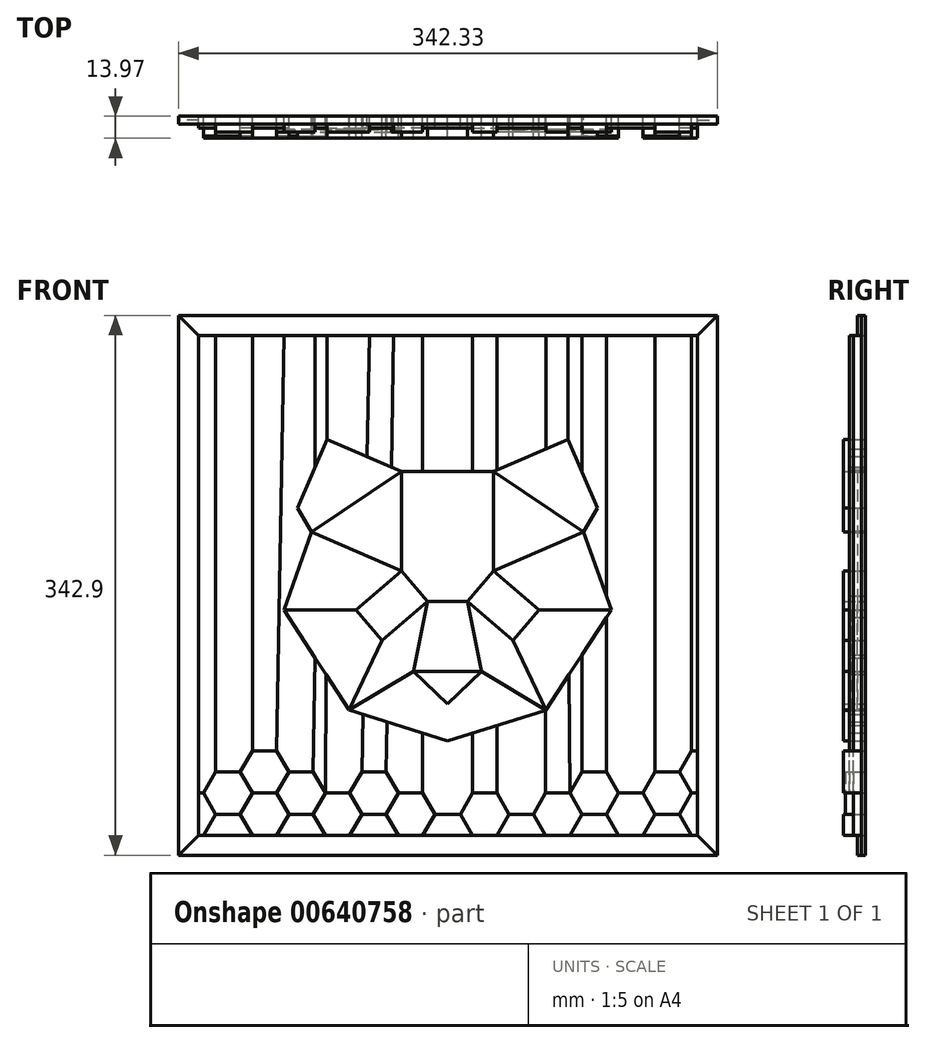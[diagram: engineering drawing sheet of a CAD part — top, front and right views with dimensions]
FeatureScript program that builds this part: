
annotation { "Feature Type Name" : "Feature", "Feature Type Description" : "" }
export const myFeature = defineFeature(function(context is Context, id is Id, definition is map)
    precondition{}
    {
        {
            var Q0;
            Q0=qCreatedBy(makeId("Front.planeOp"),FACE);
            var sketch = newSketch(context, id + "F0", { "sketchPlane" : qUnion([Q0])});
            skLineSegment(sketch, "E0.bottom", {"start": v(-170.79, 187) * mm, "end": v(171.54, 187) * mm});
            skLineSegment(sketch, "E0.top", {"start": v(-170.79, -155.9) * mm, "end": v(171.54, -155.9) * mm});
            skLineSegment(sketch, "E0.left", {"start": v(-170.79, 187) * mm, "end": v(-170.79, -155.9) * mm});
            skLineSegment(sketch, "E1.0", {"start": v(-158.09, 174.3) * mm, "end": v(158.84, 174.3) * mm});
            skLineSegment(sketch, "E2", {"start": v(-158.09, 174.3) * mm, "end": v(-158.09, -143.2) * mm});
            skLineSegment(sketch, "E3", {"start": v(-158.09, 174.3) * mm, "end": v(-170.79, 187) * mm});
            skLineSegment(sketch, "E4", {"start": v(-158.09, -143.2) * mm, "end": v(-15.07, -143.2) * mm});
            skLineSegment(sketch, "E5", {"start": v(-158.09, -143.2) * mm, "end": v(-170.79, -155.9) * mm});
            skLineSegment(sketch, "E6", {"start": v(158.84, 174.3) * mm, "end": v(158.84, -143.2) * mm});
            skLineSegment(sketch, "E7", {"start": v(158.84, 174.3) * mm, "end": v(171.54, 187) * mm});
            skLineSegment(sketch, "E8", {"start": v(158.84, -143.2) * mm, "end": v(171.54, -155.9) * mm});
            skLineSegment(sketch, "E9", {"start": v(171.54, 187) * mm, "end": v(171.54, -155.9) * mm});
            skPoint(sketch, "E10.start.orphan", {"position": v(0.38, 174.3) * mm});
            skLineSegment(sketch, "E11", {"start": v(0, -39.07) * mm, "end": v(21.5, -39.07) * mm});
            skLineSegment(sketch, "E12", {"start": v(21.5, -39.07) * mm, "end": v(0, -59.85) * mm});
            skLineSegment(sketch, "E13", {"start": v(0, 5.38) * mm, "end": v(12.7, 5.38) * mm});
            skLineSegment(sketch, "E14", {"start": v(21.5, -39.07) * mm, "end": v(12.7, 5.38) * mm});
            skLineSegment(sketch, "E15", {"start": v(0, -59.85) * mm, "end": v(0, -83.14) * mm});
            skLineSegment(sketch, "E16", {"start": v(0, -83.14) * mm, "end": v(62.58, -63.7) * mm});
            skLineSegment(sketch, "E17", {"start": v(62.58, -63.7) * mm, "end": v(21.5, -39.07) * mm});
            skLineSegment(sketch, "E18", {"start": v(29.2, 24.68) * mm, "end": v(12.7, 5.38) * mm});
            skLineSegment(sketch, "E19", {"start": v(29.2, 87.93) * mm, "end": v(29.2, 24.68) * mm});
            skLineSegment(sketch, "E20", {"start": v(29.2, 87.93) * mm, "end": v(0, 87.93) * mm});
            skLineSegment(sketch, "E21", {"start": v(29.2, 87.93) * mm, "end": v(76.43, 108.07) * mm});
            skLineSegment(sketch, "E22", {"start": v(12.7, 5.38) * mm, "end": v(41.55, -19.3) * mm});
            skLineSegment(sketch, "E23", {"start": v(41.55, -19.3) * mm, "end": v(58.06, 0) * mm});
            skLineSegment(sketch, "E24", {"start": v(58.06, 0) * mm, "end": v(29.2, 24.68) * mm});
            skLineSegment(sketch, "E25", {"start": v(62.58, -63.7) * mm, "end": v(41.55, -19.3) * mm});
            skLineSegment(sketch, "E26", {"start": v(62.58, -63.7) * mm, "end": v(103.99, 0) * mm});
            skLineSegment(sketch, "E27", {"start": v(103.99, 0) * mm, "end": v(58.06, 0) * mm});
            skLineSegment(sketch, "E28", {"start": v(103.99, 0) * mm, "end": v(86.29, 49.5) * mm});
            skLineSegment(sketch, "E29", {"start": v(86.29, 49.5) * mm, "end": v(29.2, 24.68) * mm});
            skLineSegment(sketch, "E30", {"start": v(29.2, 87.93) * mm, "end": v(86.29, 49.5) * mm});
            skLineSegment(sketch, "E31", {"start": v(86.29, 49.5) * mm, "end": v(95.32, 64.57) * mm});
            skLineSegment(sketch, "E32", {"start": v(95.32, 64.57) * mm, "end": v(76.43, 108.07) * mm});
            skPoint(sketch, "E33.MirrorP", {"position": v(-0.38, 174.3) * mm});
            skLineSegment(sketch, "E34.MirrorCS", {"start": v(0, 5.38) * mm, "end": v(-12.7, 5.38) * mm});
            skLineSegment(sketch, "E35.MirrorCS", {"start": v(-86.29, 49.5) * mm, "end": v(-95.32, 64.57) * mm});
            skLineSegment(sketch, "E36.MirrorCS", {"start": v(-29.2, 87.93) * mm, "end": v(-86.29, 49.5) * mm});
            skLineSegment(sketch, "E37.MirrorCS", {"start": v(-62.58, -63.7) * mm, "end": v(-21.5, -39.07) * mm});
            skLineSegment(sketch, "E38.MirrorCS", {"start": v(-103.99, 0) * mm, "end": v(-58.06, 0) * mm});
            skLineSegment(sketch, "E39.MirrorCS", {"start": v(-29.2, 87.93) * mm, "end": v(-29.2, 24.68) * mm});
            skLineSegment(sketch, "E40.MirrorCS", {"start": v(-62.58, -63.7) * mm, "end": v(-41.55, -19.3) * mm});
            skLineSegment(sketch, "E41.MirrorCS", {"start": v(-12.7, 5.38) * mm, "end": v(-41.55, -19.3) * mm});
            skLineSegment(sketch, "E42.MirrorCS", {"start": v(0, -39.07) * mm, "end": v(-21.5, -39.07) * mm});
            skLineSegment(sketch, "E43.MirrorCS", {"start": v(-86.29, 49.5) * mm, "end": v(-29.2, 24.68) * mm});
            skLineSegment(sketch, "E44.MirrorCS", {"start": v(-95.32, 64.57) * mm, "end": v(-76.43, 108.07) * mm});
            skLineSegment(sketch, "E45.MirrorCS", {"start": v(-21.5, -39.07) * mm, "end": v(-12.7, 5.38) * mm});
            skLineSegment(sketch, "E46.MirrorCS", {"start": v(-29.2, 87.93) * mm, "end": v(0, 87.93) * mm});
            skLineSegment(sketch, "E47.MirrorCS", {"start": v(-29.2, 87.93) * mm, "end": v(-76.43, 108.07) * mm});
            skLineSegment(sketch, "E48.MirrorCS", {"start": v(0, -83.14) * mm, "end": v(-62.58, -63.7) * mm});
            skLineSegment(sketch, "E49.MirrorCS", {"start": v(-29.2, 24.68) * mm, "end": v(-12.7, 5.38) * mm});
            skLineSegment(sketch, "E50.MirrorCS", {"start": v(-21.5, -39.07) * mm, "end": v(0, -59.85) * mm});
            skLineSegment(sketch, "E51.MirrorCS", {"start": v(-41.55, -19.3) * mm, "end": v(-58.06, 0) * mm});
            skLineSegment(sketch, "E52.MirrorCS", {"start": v(-58.06, 0) * mm, "end": v(-29.2, 24.68) * mm});
            skLineSegment(sketch, "E53.MirrorCS", {"start": v(-103.99, 0) * mm, "end": v(-86.29, 49.5) * mm});
            skLineSegment(sketch, "E54.MirrorCS", {"start": v(-62.58, -63.7) * mm, "end": v(-103.99, 0) * mm});
            skLineSegment(sketch, "E55.1", {"start": v(8.1, -129.81) * mm, "end": v(15.83, -143.2) * mm});
            skLineSegment(sketch, "E56.0", {"start": v(15.83, -116.43) * mm, "end": v(31.29, -116.43) * mm});
            skLineSegment(sketch, "E56.1", {"start": v(31.29, -116.43) * mm, "end": v(39.01, -129.81) * mm});
            skLineSegment(sketch, "E56.2", {"start": v(39.01, -129.81) * mm, "end": v(31.29, -143.2) * mm});
            skLineSegment(sketch, "E56.4", {"start": v(15.83, -143.2) * mm, "end": v(8.1, -129.81) * mm});
            skLineSegment(sketch, "E56.5", {"start": v(8.1, -129.81) * mm, "end": v(15.83, -116.43) * mm});
            skLineSegment(sketch, "E57.MirrorCS", {"start": v(54.47, -129.81) * mm, "end": v(39.01, -129.81) * mm});
            skLineSegment(sketch, "E58.MirrorCS", {"start": v(62.2, -143.2) * mm, "end": v(54.47, -129.81) * mm});
            skLineSegment(sketch, "E59.MirrorCS", {"start": v(39.01, -129.81) * mm, "end": v(54.47, -129.81) * mm});
            skLineSegment(sketch, "E60.MirrorCS", {"start": v(54.47, -129.81) * mm, "end": v(62.2, -143.2) * mm});
            skLineSegment(sketch, "E61.MirrorCS", {"start": v(77.65, -143.2) * mm, "end": v(85.38, -129.81) * mm});
            skLineSegment(sketch, "E62.MirrorCS", {"start": v(85.38, -129.81) * mm, "end": v(77.65, -116.43) * mm});
            skLineSegment(sketch, "E63.MirrorCS", {"start": v(77.65, -116.43) * mm, "end": v(62.2, -116.43) * mm});
            skLineSegment(sketch, "E64.MirrorCS", {"start": v(62.2, -116.43) * mm, "end": v(54.47, -129.81) * mm});
            skLineSegment(sketch, "E65.MirrorCS", {"start": v(100.83, -129.81) * mm, "end": v(85.38, -129.81) * mm});
            skLineSegment(sketch, "E66.MirrorCS", {"start": v(108.56, -143.2) * mm, "end": v(100.83, -129.81) * mm});
            skLineSegment(sketch, "E67.trimOffspring", {"start": v(15.83, -143.2) * mm, "end": v(158.84, -143.2) * mm});
            skLineSegment(sketch, "E68.MirrorCS", {"start": v(100.83, -129.81) * mm, "end": v(108.56, -116.43) * mm});
            skLineSegment(sketch, "E69.MirrorCS", {"start": v(108.56, -116.43) * mm, "end": v(124.01, -116.43) * mm});
            skLineSegment(sketch, "E70.MirrorCS", {"start": v(124.01, -116.43) * mm, "end": v(131.74, -129.81) * mm});
            skLineSegment(sketch, "E71.MirrorCS", {"start": v(124.01, -143.2) * mm, "end": v(131.74, -129.81) * mm});
            skLineSegment(sketch, "E72.MirrorCS", {"start": v(147.2, -129.81) * mm, "end": v(131.74, -129.81) * mm});
            skLineSegment(sketch, "E73.MirrorCS", {"start": v(147.2, -129.81) * mm, "end": v(154.92, -143.2) * mm});
            skLineSegment(sketch, "E74.MirrorCS", {"start": v(154.92, -116.43) * mm, "end": v(147.2, -129.81) * mm});
            skLineSegment(sketch, "E75.MirrorCS", {"start": v(158.84, -116.43) * mm, "end": v(154.92, -116.43) * mm});
            skLineSegment(sketch, "E76", {"start": v(15.83, -143.2) * mm, "end": v(-15.07, -143.2) * mm});
            skLineSegment(sketch, "E77.MirrorCS", {"start": v(-62.2, -143.2) * mm, "end": v(-54.47, -129.81) * mm});
            skLineSegment(sketch, "E78.MirrorCS", {"start": v(-158.09, -116.43) * mm, "end": v(-154.92, -116.43) * mm});
            skLineSegment(sketch, "E79.MirrorCS", {"start": v(-54.47, -129.81) * mm, "end": v(-39.01, -129.81) * mm});
            skLineSegment(sketch, "E80.MirrorCS", {"start": v(-54.47, -129.81) * mm, "end": v(-62.2, -143.2) * mm});
            skLineSegment(sketch, "E81.MirrorCS", {"start": v(-15.83, -143.2) * mm, "end": v(-8.1, -129.81) * mm});
            skLineSegment(sketch, "E82.MirrorCS", {"start": v(-124.01, -143.2) * mm, "end": v(-131.74, -129.81) * mm});
            skLineSegment(sketch, "E83.MirrorCS", {"start": v(-39.01, -129.81) * mm, "end": v(-31.29, -143.2) * mm});
            skLineSegment(sketch, "E84.MirrorCS", {"start": v(-31.29, -116.43) * mm, "end": v(-39.01, -129.81) * mm});
            skLineSegment(sketch, "E85.MirrorCS", {"start": v(-147.2, -129.81) * mm, "end": v(-131.74, -129.81) * mm});
            skLineSegment(sketch, "E86.MirrorCS", {"start": v(-100.83, -129.81) * mm, "end": v(-85.38, -129.81) * mm});
            skLineSegment(sketch, "E87.MirrorCS", {"start": v(-8.1, -129.81) * mm, "end": v(-15.83, -116.43) * mm});
            skLineSegment(sketch, "E88.MirrorCS", {"start": v(-108.56, -116.43) * mm, "end": v(-124.01, -116.43) * mm});
            skLineSegment(sketch, "E89.MirrorCS", {"start": v(-8.1, -129.81) * mm, "end": v(-15.83, -143.2) * mm});
            skLineSegment(sketch, "E90.MirrorCS", {"start": v(-85.38, -129.81) * mm, "end": v(-77.65, -116.43) * mm});
            skLineSegment(sketch, "E91.MirrorCS", {"start": v(-147.2, -129.81) * mm, "end": v(-154.92, -143.2) * mm});
            skLineSegment(sketch, "E92.MirrorCS", {"start": v(-77.65, -143.2) * mm, "end": v(-85.38, -129.81) * mm});
            skLineSegment(sketch, "E93.MirrorCS", {"start": v(-15.83, -116.43) * mm, "end": v(-31.29, -116.43) * mm});
            skLineSegment(sketch, "E94.MirrorCS", {"start": v(-108.56, -143.2) * mm, "end": v(-100.83, -129.81) * mm});
            skLineSegment(sketch, "E95.MirrorCS", {"start": v(-62.2, -116.43) * mm, "end": v(-54.47, -129.81) * mm});
            skLineSegment(sketch, "E96.MirrorCS", {"start": v(-100.83, -129.81) * mm, "end": v(-108.56, -116.43) * mm});
            skLineSegment(sketch, "E97.MirrorCS", {"start": v(-39.01, -129.81) * mm, "end": v(-54.47, -129.81) * mm});
            skLineSegment(sketch, "E98.MirrorCS", {"start": v(-124.01, -116.43) * mm, "end": v(-131.74, -129.81) * mm});
            skLineSegment(sketch, "E99.MirrorCS", {"start": v(-154.92, -116.43) * mm, "end": v(-147.2, -129.81) * mm});
            skLineSegment(sketch, "E100.MirrorCS", {"start": v(-77.65, -116.43) * mm, "end": v(-62.2, -116.43) * mm});
            skLineSegment(sketch, "E101", {"start": v(-8.1, -129.81) * mm, "end": v(8.1, -129.81) * mm});
            skLineSegment(sketch, "E102.MirrorCS", {"start": v(-62.2, -116.43) * mm, "end": v(-54.47, -103.04) * mm});
            skLineSegment(sketch, "E103.MirrorCS", {"start": v(-54.47, -129.81) * mm, "end": v(-62.2, -116.43) * mm});
            skLineSegment(sketch, "E104.MirrorCS", {"start": v(-39.01, -103.04) * mm, "end": v(-31.29, -116.43) * mm});
            skLineSegment(sketch, "E105.MirrorCS", {"start": v(-54.47, -103.04) * mm, "end": v(-39.01, -103.04) * mm});
            skLineSegment(sketch, "E106.MirrorCS", {"start": v(-108.56, -116.43) * mm, "end": v(-100.83, -103.04) * mm});
            skLineSegment(sketch, "E107.MirrorCS", {"start": v(-85.38, -103.04) * mm, "end": v(-77.65, -116.43) * mm});
            skLineSegment(sketch, "E108.MirrorCS", {"start": v(-100.83, -103.04) * mm, "end": v(-85.38, -103.04) * mm});
            skLineSegment(sketch, "E109.MirrorCS", {"start": v(-154.92, -116.43) * mm, "end": v(-147.2, -103.04) * mm});
            skLineSegment(sketch, "E110.MirrorCS", {"start": v(-131.74, -103.04) * mm, "end": v(-124.01, -116.43) * mm});
            skLineSegment(sketch, "E111.MirrorCS", {"start": v(-147.2, -103.04) * mm, "end": v(-131.74, -103.04) * mm});
            skLineSegment(sketch, "E112.MirrorCS", {"start": v(-131.74, -103.04) * mm, "end": v(-124.01, -89.66) * mm});
            skLineSegment(sketch, "E113.MirrorCS", {"start": v(-108.56, -89.66) * mm, "end": v(-100.83, -103.04) * mm});
            skLineSegment(sketch, "E114.MirrorCS", {"start": v(-124.01, -89.66) * mm, "end": v(-108.56, -89.66) * mm});
            skLineSegment(sketch, "E115.MirrorCS", {"start": v(124.01, -116.43) * mm, "end": v(131.74, -103.04) * mm});
            skLineSegment(sketch, "E116.MirrorCS", {"start": v(147.2, -103.04) * mm, "end": v(154.92, -116.43) * mm});
            skLineSegment(sketch, "E117.MirrorCS", {"start": v(131.74, -103.04) * mm, "end": v(147.2, -103.04) * mm});
            skLineSegment(sketch, "E118.MirrorCS", {"start": v(154.92, -89.66) * mm, "end": v(147.2, -103.04) * mm});
            skLineSegment(sketch, "E119.MirrorCS", {"start": v(158.84, -89.66) * mm, "end": v(154.92, -89.66) * mm});
            skLineSegment(sketch, "E120.0", {"start": v(85.38, -103.04) * mm, "end": v(100.83, -103.04) * mm});
            skLineSegment(sketch, "E120.1", {"start": v(100.83, -103.04) * mm, "end": v(108.56, -116.43) * mm});
            skLineSegment(sketch, "E120.5", {"start": v(77.65, -116.43) * mm, "end": v(85.38, -103.04) * mm});
            skLineSegment(sketch, "E121", {"start": v(-147.2, -103.04) * mm, "end": v(-147.2, 174.3) * mm});
            skLineSegment(sketch, "E122", {"start": v(-124.01, -89.66) * mm, "end": v(-124.01, 174.3) * mm});
            skLineSegment(sketch, "E123", {"start": v(-108.56, -89.66) * mm, "end": v(-103.99, 174.3) * mm});
            skLineSegment(sketch, "E124", {"start": v(-85.38, -103.04) * mm, "end": v(-84.12, -30.56) * mm});
            skLineSegment(sketch, "E125", {"start": v(-54.47, -103.04) * mm, "end": v(-53.83, -66.41) * mm});
            skLineSegment(sketch, "E126", {"start": v(-39.01, -103.04) * mm, "end": v(-38.46, -71.19) * mm});
            skLineSegment(sketch, "E127", {"start": v(-15.83, -116.43) * mm, "end": v(-15.83, -78.22) * mm});
            skLineSegment(sketch, "E128", {"start": v(15.83, -116.43) * mm, "end": v(15.83, -78.22) * mm});
            skLineSegment(sketch, "E129", {"start": v(31.29, -116.43) * mm, "end": v(31.29, -73.42) * mm});
            skLineSegment(sketch, "E130", {"start": v(62.2, -116.43) * mm, "end": v(62.27, -63.03) * mm});
            skLineSegment(sketch, "E131.trimOffspring", {"start": v(-51, 97.22) * mm, "end": v(-49.67, 174.3) * mm});
            skLineSegment(sketch, "E132.trimOffspring", {"start": v(-15.83, 87.93) * mm, "end": v(-15.83, 174.3) * mm});
            skLineSegment(sketch, "E133.trimOffspring", {"start": v(31.29, 88.81) * mm, "end": v(31.29, 174.3) * mm});
            skLineSegment(sketch, "E134.trimOffspring", {"start": v(15.83, 87.93) * mm, "end": v(15.83, 174.3) * mm});
            skLineSegment(sketch, "E135.trimOffspring", {"start": v(-35.66, 90.68) * mm, "end": v(-34.21, 174.3) * mm});
            skLineSegment(sketch, "E136.trimOffspring", {"start": v(62.48, 102.12) * mm, "end": v(62.58, 174.3) * mm});
            skLineSegment(sketch, "E137", {"start": v(85.38, -103.04) * mm, "end": v(85.38, -28.63) * mm});
            skLineSegment(sketch, "E138", {"start": v(100.83, -103.04) * mm, "end": v(100.83, -4.85) * mm});
            skLineSegment(sketch, "E139", {"start": v(131.74, -103.04) * mm, "end": v(131.74, 174.3) * mm});
            skLineSegment(sketch, "E140", {"start": v(154.92, -89.66) * mm, "end": v(154.92, 174.3) * mm});
            skLineSegment(sketch, "E141.trimOffspring", {"start": v(85.38, 87.47) * mm, "end": v(85.38, 174.3) * mm});
            skLineSegment(sketch, "E142.trimOffspring", {"start": v(85.38, 49.1) * mm, "end": v(85.38, 50.12) * mm});
            skLineSegment(sketch, "E143", {"start": v(-76.43, 108.07) * mm, "end": v(-76.43, 174.3) * mm});
            skLineSegment(sketch, "E144", {"start": v(76.43, 108.07) * mm, "end": v(76.43, 174.3) * mm});
            skLineSegment(sketch, "E145.trimOffspring", {"start": v(-84.12, 90.36) * mm, "end": v(-84.12, 174.3) * mm});
            skLineSegment(sketch, "E146", {"start": v(77.24, -41.14) * mm, "end": v(77.65, -116.43) * mm});
            skLineSegment(sketch, "E147.trimOffspring", {"start": v(-77.24, -41.14) * mm, "end": v(-77.65, -116.43) * mm});
            skLineSegment(sketch, "E148.trimOffspring", {"start": v(100.83, 8.83) * mm, "end": v(100.83, 174.3) * mm});
            skSolve(sketch);
        }
        {
            var Q0;
            Q0=makeQuery(id+"F0.imprint","IMPRINT",FACE,{"disambiguationData":[TD([[makeQuery(id+"F0.imprint","IMPRINT",EDGE,{"derivedFrom":sQuery(id+"F0.wireOp",EDGE,"E0.left")}),1.0]])]});
            var Q1;
            {var subQ0=sQuery(id+"F0.wireOp",EDGE,"E7");Q1=makeQuery(id+"F0.imprint","IMPRINT",FACE,{"disambiguationData":[TD([[makeQuery(id+"F0.imprint","IMPRINT",EDGE,{"derivedFrom":subQ0}),-1.0]])]});}
            extrude(context, id + "F1", {"entities" : qUnion([Q0, Q1]), "depth" : 2.54 * mm, "offsetDistance" : 25.4 * mm});
        }
        {
            var Q0;
            Q0=makeQuery(id+"F0.imprint","IMPRINT",FACE,{"disambiguationData":[TD([[makeQuery(id+"F0.imprint","IMPRINT",EDGE,{"derivedFrom":sQuery(id+"F0.wireOp",EDGE,"E0.bottom")}),-1.0]])]});
            var Q1;
            Q1=makeQuery(id+"F0.imprint","IMPRINT",FACE,{"disambiguationData":[TD([[makeQuery(id+"F0.imprint","IMPRINT",EDGE,{"derivedFrom":sQuery(id+"F0.wireOp",EDGE,"E0.top")}),1.0]])]});
            extrude(context, id + "F2", {"entities" : qUnion([Q0, Q1]), "depth" : 5.08 * mm, "offsetDistance" : 25.4 * mm});
        }
        {
            var Q0;
            {var subQ0=sQuery(id+"F0.wireOp",EDGE,"E78.MirrorCS");Q0=makeQuery(id+"F0.imprint","IMPRINT",FACE,{"disambiguationData":[TD([[makeQuery(id+"F0.imprint","IMPRINT",EDGE,{"derivedFrom":subQ0}),1.0]])]});}
            var Q1;
            Q1=makeQuery(id+"F0.imprint","IMPRINT",FACE,{"disambiguationData":[TD([[makeQuery(id+"F0.imprint","IMPRINT",EDGE,{"derivedFrom":sQuery(id+"F0.wireOp",EDGE,"E114.MirrorCS")}),1.0]])]});
            var Q2;
            {var subQ0=sQuery(id+"F0.wireOp",EDGE,"E143");Q2=makeQuery(id+"F0.imprint","IMPRINT",FACE,{"disambiguationData":[TD([[makeQuery(id+"F0.imprint","IMPRINT",EDGE,{"derivedFrom":subQ0}),1.0]])]});}
            var Q3;
            {var subQ0=sQuery(id+"F0.wireOp",EDGE,"E131.trimOffspring");Q3=makeQuery(id+"F0.imprint","IMPRINT",FACE,{"disambiguationData":[TD([[makeQuery(id+"F0.imprint","IMPRINT",EDGE,{"derivedFrom":subQ0}),-1.0]])]});}
            var Q4;
            {var subQ0=sQuery(id+"F0.wireOp",EDGE,"E132.trimOffspring");Q4=makeQuery(id+"F0.imprint","IMPRINT",FACE,{"disambiguationData":[TD([[makeQuery(id+"F0.imprint","IMPRINT",EDGE,{"derivedFrom":subQ0}),-1.0]])]});}
            var Q5;
            {var subQ0=sQuery(id+"F0.wireOp",EDGE,"E133.trimOffspring");Q5=makeQuery(id+"F0.imprint","IMPRINT",FACE,{"disambiguationData":[TD([[makeQuery(id+"F0.imprint","IMPRINT",EDGE,{"derivedFrom":subQ0}),-1.0]])]});}
            var Q6;
            {var subQ0=sQuery(id+"F0.wireOp",EDGE,"E141.trimOffspring");Q6=makeQuery(id+"F0.imprint","IMPRINT",FACE,{"disambiguationData":[TD([[makeQuery(id+"F0.imprint","IMPRINT",EDGE,{"derivedFrom":subQ0}),1.0]])]});}
            var Q7;
            Q7=makeQuery(id+"F0.imprint","IMPRINT",FACE,{"disambiguationData":[TD([[makeQuery(id+"F0.imprint","IMPRINT",EDGE,{"derivedFrom":sQuery(id+"F0.wireOp",EDGE,"E69.MirrorCS")}),1.0]])]});
            var Q8;
            Q8=makeQuery(id+"F0.imprint","IMPRINT",FACE,{"disambiguationData":[TD([[makeQuery(id+"F0.imprint","IMPRINT",EDGE,{"derivedFrom":sQuery(id+"F0.wireOp",EDGE,"E120.5")}),1.0]])]});
            var Q9;
            Q9=makeQuery(id+"F0.imprint","IMPRINT",FACE,{"disambiguationData":[TD([[makeQuery(id+"F0.imprint","IMPRINT",EDGE,{"derivedFrom":sQuery(id+"F0.wireOp",EDGE,"E56.1")}),1.0]])]});
            var Q10;
            Q10=makeQuery(id+"F0.imprint","IMPRINT",FACE,{"disambiguationData":[TD([[makeQuery(id+"F0.imprint","IMPRINT",EDGE,{"derivedFrom":sQuery(id+"F0.wireOp",EDGE,"E56.5")}),1.0]])]});
            var Q11;
            Q11=makeQuery(id+"F0.imprint","IMPRINT",FACE,{"disambiguationData":[TD([[makeQuery(id+"F0.imprint","IMPRINT",EDGE,{"derivedFrom":sQuery(id+"F0.wireOp",EDGE,"E105.MirrorCS")}),1.0]])]});
            var Q12;
            Q12=makeQuery(id+"F0.imprint","IMPRINT",FACE,{"disambiguationData":[TD([[makeQuery(id+"F0.imprint","IMPRINT",EDGE,{"derivedFrom":sQuery(id+"F0.wireOp",EDGE,"E107.MirrorCS")}),1.0]])]});
            var Q13;
            {var subQ4=sQuery(id+"F0.wireOp",EDGE,"E119.MirrorCS");Q13=makeQuery(id+"F0.imprint","IMPRINT",FACE,{"disambiguationData":[TD([[makeQuery(id+"F0.imprint","IMPRINT",EDGE,{"derivedFrom":subQ4}),-1.0]])]});}
            extrude(context, id + "F3", {"entities" : qUnion([Q0, Q1, Q2, Q3, Q4, Q5, Q6, Q7, Q8, Q9, Q10, Q11, Q12, Q13]), "depth" : 7.62 * mm, "offsetDistance" : 25.4 * mm});
        }
        {
            var Q0;
            Q0=makeQuery(id+"F0.imprint","IMPRINT",FACE,{"disambiguationData":[TD([[makeQuery(id+"F0.imprint","IMPRINT",EDGE,{"derivedFrom":sQuery(id+"F0.wireOp",EDGE,"E111.MirrorCS")}),1.0]])]});
            var Q1;
            {var subQ1=sQuery(id+"F0.wireOp",EDGE,"E35.MirrorCS");Q1=makeQuery(id+"F0.imprint","IMPRINT",FACE,{"disambiguationData":[TD([[makeQuery(id+"F0.imprint","IMPRINT",EDGE,{"derivedFrom":subQ1}),1.0]])]});}
            var Q2;
            {var subQ0=sQuery(id+"F0.wireOp",EDGE,"E131.trimOffspring");Q2=makeQuery(id+"F0.imprint","IMPRINT",FACE,{"disambiguationData":[TD([[makeQuery(id+"F0.imprint","IMPRINT",EDGE,{"derivedFrom":subQ0}),1.0]])]});}
            var Q3;
            {var subQ0=sQuery(id+"F0.wireOp",EDGE,"E132.trimOffspring");Q3=makeQuery(id+"F0.imprint","IMPRINT",FACE,{"disambiguationData":[TD([[makeQuery(id+"F0.imprint","IMPRINT",EDGE,{"derivedFrom":subQ0}),1.0]])]});}
            var Q4;
            {var subQ0=sQuery(id+"F0.wireOp",EDGE,"E133.trimOffspring");Q4=makeQuery(id+"F0.imprint","IMPRINT",FACE,{"disambiguationData":[TD([[makeQuery(id+"F0.imprint","IMPRINT",EDGE,{"derivedFrom":subQ0}),1.0]])]});}
            var Q5;
            {var subQ0=sQuery(id+"F0.wireOp",EDGE,"E136.trimOffspring");Q5=makeQuery(id+"F0.imprint","IMPRINT",FACE,{"disambiguationData":[TD([[makeQuery(id+"F0.imprint","IMPRINT",EDGE,{"derivedFrom":subQ0}),-1.0]])]});}
            var Q6;
            {var subQ1=sQuery(id+"F0.wireOp",EDGE,"E31");Q6=makeQuery(id+"F0.imprint","IMPRINT",FACE,{"disambiguationData":[TD([[makeQuery(id+"F0.imprint","IMPRINT",EDGE,{"derivedFrom":subQ1}),-1.0]])]});}
            var Q7;
            Q7=makeQuery(id+"F0.imprint","IMPRINT",FACE,{"disambiguationData":[TD([[makeQuery(id+"F0.imprint","IMPRINT",EDGE,{"derivedFrom":sQuery(id+"F0.wireOp",EDGE,"E117.MirrorCS")}),1.0]])]});
            var Q8;
            Q8=makeQuery(id+"F0.imprint","IMPRINT",FACE,{"disambiguationData":[TD([[makeQuery(id+"F0.imprint","IMPRINT",EDGE,{"derivedFrom":sQuery(id+"F0.wireOp",EDGE,"E120.0")}),1.0]])]});
            var Q9;
            {var subQ0=sQuery(id+"F0.wireOp",EDGE,"E63.MirrorCS");Q9=makeQuery(id+"F0.imprint","IMPRINT",FACE,{"disambiguationData":[TD([[makeQuery(id+"F0.imprint","IMPRINT",EDGE,{"derivedFrom":subQ0}),-1.0]])]});}
            var Q10;
            Q10=makeQuery(id+"F0.imprint","IMPRINT",FACE,{"disambiguationData":[TD([[makeQuery(id+"F0.imprint","IMPRINT",EDGE,{"derivedFrom":sQuery(id+"F0.wireOp",EDGE,"E56.0")}),1.0]])]});
            var Q11;
            Q11=makeQuery(id+"F0.imprint","IMPRINT",FACE,{"disambiguationData":[TD([[makeQuery(id+"F0.imprint","IMPRINT",EDGE,{"derivedFrom":sQuery(id+"F0.wireOp",EDGE,"E93.MirrorCS")}),-1.0]])]});
            var Q12;
            Q12=makeQuery(id+"F0.imprint","IMPRINT",FACE,{"disambiguationData":[TD([[makeQuery(id+"F0.imprint","IMPRINT",EDGE,{"derivedFrom":sQuery(id+"F0.wireOp",EDGE,"E100.MirrorCS")}),1.0]])]});
            extrude(context, id + "F4", {"entities" : qUnion([Q0, Q1, Q2, Q3, Q4, Q5, Q6, Q7, Q8, Q9, Q10, Q11, Q12]), "depth" : 10.16 * mm, "offsetDistance" : 25.4 * mm});
        }
        {
            var Q0;
            {var subQ0=sQuery(id+"F0.wireOp",EDGE,"E78.MirrorCS");Q0=makeQuery(id+"F0.imprint","IMPRINT",FACE,{"disambiguationData":[TD([[makeQuery(id+"F0.imprint","IMPRINT",EDGE,{"derivedFrom":subQ0}),-1.0]])]});}
            var Q1;
            {var subQ1=sQuery(id+"F0.wireOp",EDGE,"E82.MirrorCS");Q1=makeQuery(id+"F0.imprint","IMPRINT",FACE,{"disambiguationData":[TD([[makeQuery(id+"F0.imprint","IMPRINT",EDGE,{"derivedFrom":subQ1}),-1.0]])]});}
            var Q2;
            Q2=makeQuery(id+"F0.imprint","IMPRINT",FACE,{"disambiguationData":[TD([[makeQuery(id+"F0.imprint","IMPRINT",EDGE,{"derivedFrom":sQuery(id+"F0.wireOp",EDGE,"E90.MirrorCS")}),-1.0]])]});
            var Q3;
            {var subQ1=sQuery(id+"F0.wireOp",EDGE,"E83.MirrorCS");Q3=makeQuery(id+"F0.imprint","IMPRINT",FACE,{"disambiguationData":[TD([[makeQuery(id+"F0.imprint","IMPRINT",EDGE,{"derivedFrom":subQ1}),1.0]])]});}
            var Q4;
            Q4=makeQuery(id+"F0.imprint","IMPRINT",FACE,{"disambiguationData":[TD([[makeQuery(id+"F0.imprint","IMPRINT",EDGE,{"derivedFrom":sQuery(id+"F0.wireOp",EDGE,"E56.0")}),-1.0]])]});
            var Q5;
            {var subQ1=sQuery(id+"F0.wireOp",EDGE,"E60.MirrorCS");Q5=makeQuery(id+"F0.imprint","IMPRINT",FACE,{"disambiguationData":[TD([[makeQuery(id+"F0.imprint","IMPRINT",EDGE,{"derivedFrom":subQ1}),1.0]])]});}
            var Q6;
            {var subQ1=sQuery(id+"F0.wireOp",EDGE,"E66.MirrorCS");Q6=makeQuery(id+"F0.imprint","IMPRINT",FACE,{"disambiguationData":[TD([[makeQuery(id+"F0.imprint","IMPRINT",EDGE,{"derivedFrom":subQ1}),-1.0]])]});}
            var Q7;
            {var subQ0=sQuery(id+"F0.wireOp",EDGE,"E73.MirrorCS");Q7=makeQuery(id+"F0.imprint","IMPRINT",FACE,{"disambiguationData":[TD([[makeQuery(id+"F0.imprint","IMPRINT",EDGE,{"derivedFrom":subQ0}),1.0]])]});}
            extrude(context, id + "F5", {"entities" : qUnion([Q0, Q1, Q2, Q3, Q4, Q5, Q6, Q7]), "depth" : 7.62 * mm, "offsetDistance" : 25.4 * mm});
        }
        {
            var Q0;
            Q0=makeQuery(id+"F0.imprint","IMPRINT",FACE,{"disambiguationData":[TD([[makeQuery(id+"F0.imprint","IMPRINT",EDGE,{"derivedFrom":sQuery(id+"F0.wireOp",EDGE,"E85.MirrorCS")}),1.0]])]});
            var Q1;
            Q1=makeQuery(id+"F0.imprint","IMPRINT",FACE,{"disambiguationData":[TD([[makeQuery(id+"F0.imprint","IMPRINT",EDGE,{"derivedFrom":sQuery(id+"F0.wireOp",EDGE,"E86.MirrorCS")}),1.0]])]});
            var Q2;
            Q2=makeQuery(id+"F0.imprint","IMPRINT",FACE,{"disambiguationData":[TD([[makeQuery(id+"F0.imprint","IMPRINT",EDGE,{"derivedFrom":sQuery(id+"F0.wireOp",EDGE,"E97.MirrorCS")}),-1.0]])]});
            var Q3;
            Q3=makeQuery(id+"F0.imprint","IMPRINT",FACE,{"disambiguationData":[TD([[makeQuery(id+"F0.imprint","IMPRINT",EDGE,{"derivedFrom":sQuery(id+"F0.wireOp",EDGE,"E62.MirrorCS")}),-1.0]])]});
            var Q4;
            Q4=makeQuery(id+"F0.imprint","IMPRINT",FACE,{"disambiguationData":[TD([[makeQuery(id+"F0.imprint","IMPRINT",EDGE,{"derivedFrom":sQuery(id+"F0.wireOp",EDGE,"E70.MirrorCS")}),1.0]])]});
            extrude(context, id + "F6", {"entities" : qUnion([Q0, Q1, Q2, Q3, Q4]), "depth" : 12.7 * mm, "offsetDistance" : 25.4 * mm});
        }
        {
            var Q0;
            {var subQ0=sQuery(id+"F0.wireOp",EDGE,"E82.MirrorCS");Q0=makeQuery(id+"F0.imprint","IMPRINT",FACE,{"disambiguationData":[TD([[makeQuery(id+"F0.imprint","IMPRINT",EDGE,{"derivedFrom":subQ0}),1.0]])]});}
            var Q1;
            Q1=makeQuery(id+"F0.imprint","IMPRINT",FACE,{"disambiguationData":[TD([[makeQuery(id+"F0.imprint","IMPRINT",EDGE,{"derivedFrom":sQuery(id+"F0.wireOp",EDGE,"E88.MirrorCS")}),-1.0]])]});
            var Q2;
            Q2=makeQuery(id+"F0.imprint","IMPRINT",FACE,{"disambiguationData":[TD([[makeQuery(id+"F0.imprint","IMPRINT",EDGE,{"derivedFrom":sQuery(id+"F0.wireOp",EDGE,"E86.MirrorCS")}),-1.0]])]});
            var Q3;
            {var subQ0=sQuery(id+"F0.wireOp",EDGE,"E83.MirrorCS");Q3=makeQuery(id+"F0.imprint","IMPRINT",FACE,{"disambiguationData":[TD([[makeQuery(id+"F0.imprint","IMPRINT",EDGE,{"derivedFrom":subQ0}),-1.0]])]});}
            var Q4;
            Q4=makeQuery(id+"F0.imprint","IMPRINT",FACE,{"disambiguationData":[TD([[makeQuery(id+"F0.imprint","IMPRINT",EDGE,{"derivedFrom":sQuery(id+"F0.wireOp",EDGE,"E56.4")}),1.0]])]});
            var Q5;
            {var subQ0=sQuery(id+"F0.wireOp",EDGE,"E56.2");Q5=makeQuery(id+"F0.imprint","IMPRINT",FACE,{"disambiguationData":[TD([[makeQuery(id+"F0.imprint","IMPRINT",EDGE,{"derivedFrom":subQ0}),1.0]])]});}
            var Q6;
            {var subQ0=sQuery(id+"F0.wireOp",EDGE,"E61.MirrorCS");Q6=makeQuery(id+"F0.imprint","IMPRINT",FACE,{"disambiguationData":[TD([[makeQuery(id+"F0.imprint","IMPRINT",EDGE,{"derivedFrom":subQ0}),-1.0]])]});}
            var Q7;
            {var subQ0=sQuery(id+"F0.wireOp",EDGE,"E71.MirrorCS");Q7=makeQuery(id+"F0.imprint","IMPRINT",FACE,{"disambiguationData":[TD([[makeQuery(id+"F0.imprint","IMPRINT",EDGE,{"derivedFrom":subQ0}),-1.0]])]});}
            var Q8;
            {var subQ0=sQuery(id+"F0.wireOp",EDGE,"E75.MirrorCS");Q8=makeQuery(id+"F0.imprint","IMPRINT",FACE,{"disambiguationData":[TD([[makeQuery(id+"F0.imprint","IMPRINT",EDGE,{"derivedFrom":subQ0}),-1.0]])]});}
            var Q9;
            Q9=makeQuery(id+"F0.imprint","IMPRINT",FACE,{"disambiguationData":[TD([[makeQuery(id+"F0.imprint","IMPRINT",EDGE,{"derivedFrom":sQuery(id+"F0.wireOp",EDGE,"E11")}),1.0]])]});
            var Q10;
            Q10=makeQuery(id+"F0.imprint","IMPRINT",FACE,{"disambiguationData":[TD([[makeQuery(id+"F0.imprint","IMPRINT",EDGE,{"derivedFrom":sQuery(id+"F0.wireOp",EDGE,"E18")}),1.0]])]});
            var Q11;
            Q11=makeQuery(id+"F0.imprint","IMPRINT",FACE,{"disambiguationData":[TD([[makeQuery(id+"F0.imprint","IMPRINT",EDGE,{"derivedFrom":sQuery(id+"F0.wireOp",EDGE,"E41.MirrorCS")}),-1.0]])]});
            var Q12;
            {var subQ8=sQuery(id+"F0.wireOp",EDGE,"E31");Q12=makeQuery(id+"F0.imprint","IMPRINT",FACE,{"disambiguationData":[TD([[makeQuery(id+"F0.imprint","IMPRINT",EDGE,{"derivedFrom":subQ8}),1.0]])]});}
            var Q13;
            {var subQ1=sQuery(id+"F0.wireOp",EDGE,"E35.MirrorCS");Q13=makeQuery(id+"F0.imprint","IMPRINT",FACE,{"disambiguationData":[TD([[makeQuery(id+"F0.imprint","IMPRINT",EDGE,{"derivedFrom":subQ1}),-1.0]])]});}
            var Q14;
            {var subQ4=sQuery(id+"F0.wireOp",EDGE,"E37.MirrorCS");Q14=makeQuery(id+"F0.imprint","IMPRINT",FACE,{"disambiguationData":[TD([[makeQuery(id+"F0.imprint","IMPRINT",EDGE,{"derivedFrom":subQ4}),-1.0]])]});}
            var Q15;
            {var subQ8=sQuery(id+"F0.wireOp",EDGE,"E12");Q15=makeQuery(id+"F0.imprint","IMPRINT",FACE,{"disambiguationData":[TD([[makeQuery(id+"F0.imprint","IMPRINT",EDGE,{"derivedFrom":subQ8}),1.0]])]});}
            extrude(context, id + "F7", {"entities" : qUnion([Q0, Q1, Q2, Q3, Q4, Q5, Q6, Q7, Q8, Q9, Q10, Q11, Q12, Q13, Q14, Q15]), "depth" : 13.97 * mm, "offsetDistance" : 25.4 * mm});
        }
        {
            var Q0;
            Q0=makeQuery(id+"F0.imprint","IMPRINT",FACE,{"disambiguationData":[TD([[makeQuery(id+"F0.imprint","IMPRINT",EDGE,{"derivedFrom":sQuery(id+"F0.wireOp",EDGE,"E13")}),1.0]])]});
            var Q1;
            Q1=makeQuery(id+"F0.imprint","IMPRINT",FACE,{"disambiguationData":[TD([[makeQuery(id+"F0.imprint","IMPRINT",EDGE,{"derivedFrom":sQuery(id+"F0.wireOp",EDGE,"E37.MirrorCS")}),1.0]])]});
            var Q2;
            {var subQ6=sQuery(id+"F0.wireOp",EDGE,"E14");Q2=makeQuery(id+"F0.imprint","IMPRINT",FACE,{"disambiguationData":[TD([[makeQuery(id+"F0.imprint","IMPRINT",EDGE,{"derivedFrom":subQ6}),-1.0]])]});}
            var Q3;
            Q3=makeQuery(id+"F0.imprint","IMPRINT",FACE,{"disambiguationData":[TD([[makeQuery(id+"F0.imprint","IMPRINT",EDGE,{"derivedFrom":sQuery(id+"F0.wireOp",EDGE,"E11")}),-1.0]])]});
            extrude(context, id + "F8", {"entities" : qUnion([Q0, Q1, Q2, Q3]), "depth" : 5.08 * mm, "offsetDistance" : 25.4 * mm});
        }
        {
            var Q0;
            Q0=makeQuery(id+"F0.imprint","IMPRINT",FACE,{"disambiguationData":[TD([[makeQuery(id+"F0.imprint","IMPRINT",EDGE,{"derivedFrom":sQuery(id+"F0.wireOp",EDGE,"E38.MirrorCS")}),1.0]])]});
            var Q1;
            {var subQ5=sQuery(id+"F0.wireOp",EDGE,"E24");Q1=makeQuery(id+"F0.imprint","IMPRINT",FACE,{"disambiguationData":[TD([[makeQuery(id+"F0.imprint","IMPRINT",EDGE,{"derivedFrom":subQ5}),-1.0]])]});}
            extrude(context, id + "F9", {"entities" : qUnion([Q0, Q1]), "depth" : 10.16 * mm, "offsetDistance" : 25.4 * mm});
        }
        {
            var Q0;
            Q0=makeQuery(id+"F0.imprint","IMPRINT",FACE,{"disambiguationData":[TD([[makeQuery(id+"F0.imprint","IMPRINT",EDGE,{"derivedFrom":sQuery(id+"F0.wireOp",EDGE,"E36.MirrorCS")}),1.0]])]});
            var Q1;
            {var subQ3=sQuery(id+"F0.wireOp",EDGE,"E38.MirrorCS");Q1=makeQuery(id+"F0.imprint","IMPRINT",FACE,{"disambiguationData":[TD([[makeQuery(id+"F0.imprint","IMPRINT",EDGE,{"derivedFrom":subQ3}),-1.0]])]});}
            var Q2;
            {var subQ0=sQuery(id+"F0.wireOp",EDGE,"E19");Q2=makeQuery(id+"F0.imprint","IMPRINT",FACE,{"disambiguationData":[TD([[makeQuery(id+"F0.imprint","IMPRINT",EDGE,{"derivedFrom":subQ0}),1.0]])]});}
            var Q3;
            {var subQ4=sQuery(id+"F0.wireOp",EDGE,"E23");Q3=makeQuery(id+"F0.imprint","IMPRINT",FACE,{"disambiguationData":[TD([[makeQuery(id+"F0.imprint","IMPRINT",EDGE,{"derivedFrom":subQ4}),-1.0]])]});}
            extrude(context, id + "F10", {"entities" : qUnion([Q0, Q1, Q2, Q3]), "depth" : 8.38 * mm, "offsetDistance" : 25.4 * mm});
        }
    });
